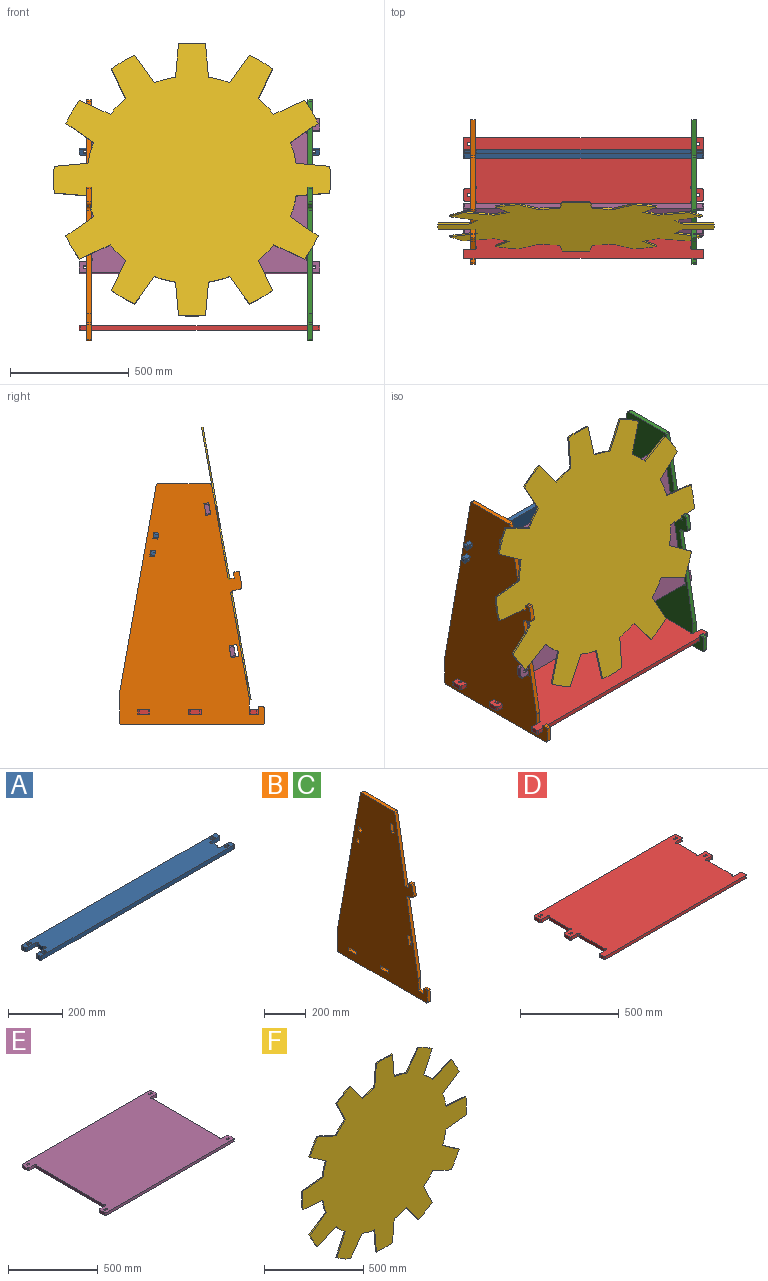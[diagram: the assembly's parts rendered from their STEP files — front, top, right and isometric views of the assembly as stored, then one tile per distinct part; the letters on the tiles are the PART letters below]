
ASSEMBLY  parts=6 mates=11
PART A: 50 faces, bbox 1016x101.6x19.1 mm
  f0: plane 1016x101.6mm, normal (0,0,-1), area 96811.6mm2, adj f2,f3,f4,f5,f6,f7,f8,f9
  f1: plane 1016x101.6mm, normal (0,0,1), area 96811.6mm2, adj f2,f3,f4,f5,f6,f7,f8,f9
  f2: plane 25.4x19.05mm, normal (1,0,0), area 483.9mm2, adj f0,f1,f3,f25
  f3: cylinder r=6.35mm len=19.05mm, axis (0,0,-1), area 380mm2, adj f0,f1,f2,f4
  f4: plane 44.45x19.05mm, normal (0,-1,0), area 846.8mm2, adj f0,f1,f3,f5
  f5: cylinder r=6.35mm len=19.05mm, axis (0,0,-1), area 190mm2, adj f0,f1,f4,f6
  f6: plane 19.05x12.7mm, normal (1,0,0), area 241.9mm2, adj f0,f1,f5,f7
  f7: cylinder r=6.35mm len=19.05mm, axis (0,0,-1), area 190mm2, adj f0,f1,f6,f8
  f8: plane 1003.3x19.05mm, normal (0,1,0), area 19112.9mm2, adj f0,f1,f7,f9
  f9: cylinder r=6.35mm len=19.05mm, axis (0,0,-1), area 190mm2, adj f0,f1,f8,f10
  f10: plane 19.05x12.7mm, normal (-1,0,0), area 241.9mm2, adj f0,f1,f9,f11
  f11: cylinder r=6.35mm len=19.05mm, axis (0,0,-1), area 190mm2, adj f0,f1,f10,f12
  f12: plane 44.45x19.05mm, normal (0,-1,0), area 846.8mm2, adj f0,f1,f11,f13
  f13: cylinder r=6.35mm len=19.05mm, axis (0,0,-1), area 380mm2, adj f0,f1,f12,f14
  f14: plane 25.4x19.05mm, normal (-1,0,0), area 483.9mm2, adj f0,f1,f13,f15
  f15: cylinder r=6.35mm len=19.05mm, axis (0,0,-1), area 380mm2, adj f0,f1,f14,f16
  f16: plane 44.45x19.05mm, normal (0,1,0), area 846.8mm2, adj f0,f1,f15,f17
  f17: cylinder r=6.35mm len=19.05mm, axis (0,0,-1), area 190mm2, adj f0,f1,f16,f18
  f18: plane 19.05x12.7mm, normal (-1,0,0), area 241.9mm2, adj f0,f1,f17,f19
  f19: cylinder r=6.35mm len=19.05mm, axis (0,0,-1), area 190mm2, adj f0,f1,f18,f20
  f20: plane 1003.3x19.05mm, normal (0,-1,0), area 19112.9mm2, adj f0,f1,f19,f21
  f21: cylinder r=6.35mm len=19.05mm, axis (0,0,-1), area 190mm2, adj f0,f1,f20,f22
  f22: plane 19.05x12.7mm, normal (1,0,0), area 241.9mm2, adj f0,f1,f21,f23
  f23: cylinder r=6.35mm len=19.05mm, axis (0,0,-1), area 190mm2, adj f0,f1,f22,f24
  f24: plane 44.45x19.05mm, normal (0,1,0), area 846.8mm2, adj f0,f1,f23,f25
  f25: cylinder r=6.35mm len=19.05mm, axis (0,0,-1), area 380mm2, adj f0,f1,f2,f24
  f26: plane 19.05x12.7mm, normal (0,-1,0), area 241.9mm2, adj f0,f1,f29,f49
  f27: plane 19.05x6.35mm, normal (1,0,0), area 121mm2, adj f0,f1,f48,f49
  f28: plane 19.05x12.7mm, normal (0,1,0), area 241.9mm2, adj f0,f1,f29,f48
  f29: cylinder r=6.35mm len=19.05mm, axis (0,0,1), area 380mm2, adj f0,f1,f26,f28
  f30: plane 19.05x6.35mm, normal (-1,0,0), area 121mm2, adj f0,f1,f46,f47
  f31: plane 19.05x12.7mm, normal (0,-1,0), area 241.9mm2, adj f0,f1,f32,f47
  f32: cylinder r=6.35mm len=19.05mm, axis (0,0,1), area 380mm2, adj f0,f1,f31,f33
  f33: plane 19.05x12.7mm, normal (0,1,0), area 241.9mm2, adj f0,f1,f32,f46
  f34: plane 19.05x6.35mm, normal (-1,0,0), area 121mm2, adj f0,f1,f44,f45
  f35: plane 19.05x12.7mm, normal (0,-1,0), area 241.9mm2, adj f0,f1,f36,f45
  f36: cylinder r=6.35mm len=19.05mm, axis (0,0,1), area 380mm2, adj f0,f1,f35,f37
  f37: plane 19.05x12.7mm, normal (0,1,0), area 241.9mm2, adj f0,f1,f36,f44
  f38: plane 19.05x12.7mm, normal (0,-1,0), area 241.9mm2, adj f0,f1,f41,f43
  f39: plane 19.05x6.35mm, normal (1,0,0), area 121mm2, adj f0,f1,f42,f43
  f40: plane 19.05x12.7mm, normal (0,1,0), area 241.9mm2, adj f0,f1,f41,f42
  f41: cylinder r=6.35mm len=19.05mm, axis (0,0,1), area 380mm2, adj f0,f1,f38,f40
  f42: cylinder r=1.59mm len=19.05mm, axis (0,0,1), area 95mm2, adj f0,f1,f39,f40
  f43: cylinder r=1.59mm len=19.05mm, axis (0,0,1), area 95mm2, adj f0,f1,f38,f39
  f44: cylinder r=1.59mm len=19.05mm, axis (0,0,1), area 95mm2, adj f0,f1,f34,f37
  f45: cylinder r=1.59mm len=19.05mm, axis (0,0,1), area 95mm2, adj f0,f1,f34,f35
  f46: cylinder r=1.59mm len=19.05mm, axis (0,0,1), area 95mm2, adj f0,f1,f30,f33
  f47: cylinder r=1.59mm len=19.05mm, axis (0,0,1), area 95mm2, adj f0,f1,f30,f31
  f48: cylinder r=1.59mm len=19.05mm, axis (0,0,1), area 95mm2, adj f0,f1,f27,f28
  f49: cylinder r=1.59mm len=19.05mm, axis (0,0,1), area 95mm2, adj f0,f1,f26,f27
PART B: 54 faces, bbox 19.1x609.6x1016 mm
  f0: plane 1016x609.6mm, normal (1,0,0), area 417121.7mm2, adj f2,f3,f4,f5,f6,f7,f8,f9
  f1: plane 1016x609.6mm, normal (-1,0,0), area 417121.7mm2, adj f2,f3,f4,f5,f6,f7,f8,f9
  f2: plane 50.8x19.05mm, normal (0,0,1), area 967.7mm2, adj f0,f1,f3,f28
  f3: plane 20.32x19.05mm, normal (0,1,0), area 387.1mm2, adj f0,f1,f2,f4
  f4: plane 50.8x19.05mm, normal (0,0,-1), area 967.7mm2, adj f0,f1,f3,f28
  f5: plane 19.05x19.05mm, normal (0,1,0), area 362.9mm2, adj f0,f1,f6,f26
  f6: plane 50.8x19.05mm, normal (0,0,-1), area 967.7mm2, adj f0,f1,f5,f7
  f7: plane 19.05x19.05mm, normal (0,-1,0), area 362.9mm2, adj f0,f1,f6,f26
  f8: plane 221.9x19.05mm, normal (0,0,1), area 4227.3mm2, adj f0,f1,f45,f53
  f9: plane 396.94x69.99mm, normal (0,-0.98,0.17), area 7678.4mm2, adj f0,f1,f10,f45
  f10: plane 25.01x19.05mm, normal (0,0.17,0.98), area 483.9mm2, adj f0,f1,f9,f11
  f11: plane 19.05x18.76mm, normal (0,0.98,-0.17), area 362.9mm2, adj f0,f1,f10,f46
  f12: plane 19.05x12.51mm, normal (0,0.17,0.98), area 241.9mm2, adj f0,f1,f46,f47
  f13: plane 56.28x19.05mm, normal (0,-0.98,0.17), area 1088.7mm2, adj f0,f1,f14,f47
  f14: cylinder r=12.7mm len=19.05mm, axis (-1,0,0), area 380mm2, adj f0,f1,f13,f15
  f15: plane 25.01x19.05mm, normal (0,-0.17,-0.98), area 483.9mm2, adj f0,f1,f14,f16
  f16: cylinder r=12.7mm len=19.05mm, axis (-1,0,0), area 380mm2, adj f0,f1,f15,f17
  f17: plane 435.93x76.87mm, normal (0,-0.98,0.17), area 8432.5mm2, adj f0,f1,f16,f18
  f18: cylinder r=12.7mm len=19.05mm, axis (-1,0,0), area 42.2mm2, adj f0,f1,f17,f19
  f19: plane 68.69x19.05mm, normal (0,-1,0), area 1308.6mm2, adj f0,f1,f18,f20
  f20: plane 38.1x19.05mm, normal (0,0,1), area 725.8mm2, adj f0,f1,f19,f21
  f21: plane 25.4x19.05mm, normal (0,1,0), area 483.9mm2, adj f0,f1,f20,f48
  f22: plane 19.05x12.7mm, normal (0,0,1), area 241.9mm2, adj f0,f1,f48,f49
  f23: plane 63.5x19.05mm, normal (0,-1,0), area 1209.7mm2, adj f0,f1,f49,f50
  f24: plane 596.9x19.05mm, normal (0,0,-1), area 11370.9mm2, adj f0,f1,f50,f51
  f25: plane 132.67x19.05mm, normal (0,1,0), area 2527.3mm2, adj f0,f1,f51,f52
  f26: plane 50.8x19.05mm, normal (0,0,1), area 967.7mm2, adj f0,f1,f5,f7
  f27: plane 870.63x153.52mm, normal (0,0.98,0.17), area 16841.4mm2, adj f0,f1,f52,f53
  f28: plane 20.32x19.05mm, normal (0,-1,0), area 387.1mm2, adj f0,f1,f2,f4
  f29: plane 20.01x19.05mm, normal (0,-0.17,-0.98), area 387.1mm2, adj f0,f1,f30,f32
  f30: plane 50.03x19.05mm, normal (0,0.98,-0.17), area 967.7mm2, adj f0,f1,f29,f31
  f31: plane 20.01x19.05mm, normal (0,0.17,0.98), area 387.1mm2, adj f0,f1,f30,f32
  f32: plane 50.03x19.05mm, normal (0,-0.98,0.17), area 967.7mm2, adj f0,f1,f29,f31
  f33: plane 20.01x19.05mm, normal (0,0.17,-0.98), area 387.1mm2, adj f0,f1,f34,f36
  f34: plane 25.01x19.05mm, normal (0,0.98,0.17), area 483.9mm2, adj f0,f1,f33,f35
  f35: plane 20.01x19.05mm, normal (0,-0.17,0.98), area 387.1mm2, adj f0,f1,f34,f36
  f36: plane 25.01x19.05mm, normal (0,-0.98,-0.17), area 483.9mm2, adj f0,f1,f33,f35
  f37: plane 20.01x19.05mm, normal (0,0.17,-0.98), area 387.1mm2, adj f0,f1,f38,f40
  f38: plane 25.01x19.05mm, normal (0,0.98,0.17), area 483.9mm2, adj f0,f1,f37,f39
  f39: plane 20.01x19.05mm, normal (0,-0.17,0.98), area 387.1mm2, adj f0,f1,f38,f40
  f40: plane 25.01x19.05mm, normal (0,-0.98,-0.17), area 483.9mm2, adj f0,f1,f37,f39
  f41: plane 20.01x19.05mm, normal (0,-0.17,-0.98), area 387.1mm2, adj f0,f1,f42,f44
  f42: plane 50.03x19.05mm, normal (0,0.98,-0.17), area 967.7mm2, adj f0,f1,f41,f43
  f43: plane 20.01x19.05mm, normal (0,0.17,0.98), area 387.1mm2, adj f0,f1,f42,f44
  f44: plane 50.03x19.05mm, normal (0,-0.98,0.17), area 967.7mm2, adj f0,f1,f41,f43
  f45: cylinder r=6.35mm len=19.05mm, axis (-1,0,0), area 168.9mm2, adj f0,f1,f8,f9
  f46: cylinder r=6.35mm len=19.05mm, axis (-1,0,0), area 190mm2, adj f0,f1,f11,f12
  f47: cylinder r=6.35mm len=19.05mm, axis (-1,0,0), area 190mm2, adj f0,f1,f12,f13
  f48: cylinder r=6.35mm len=19.05mm, axis (-1,0,0), area 190mm2, adj f0,f1,f21,f22
  f49: cylinder r=6.35mm len=19.05mm, axis (1,0,0), area 190mm2, adj f0,f1,f22,f23
  f50: cylinder r=6.35mm len=19.05mm, axis (1,0,0), area 190mm2, adj f0,f1,f23,f24
  f51: cylinder r=6.35mm len=19.05mm, axis (1,0,0), area 190mm2, adj f0,f1,f24,f25
  f52: cylinder r=6.35mm len=19.05mm, axis (1,0,0), area 21.1mm2, adj f0,f1,f25,f27
  f53: cylinder r=6.35mm len=19.05mm, axis (-1,0,0), area 168.9mm2, adj f0,f1,f8,f27
PART C: same geometry as B
PART D: 66 faces, bbox 1016x508x19.1 mm
  f0: plane 1016x508mm, normal (0,0,1), area 477168mm2, adj f2,f3,f4,f5,f6,f7,f8,f9
  f1: plane 1016x508mm, normal (0,0,-1), area 477168mm2, adj f2,f3,f4,f5,f6,f7,f8,f9
  f2: cylinder r=6.35mm len=19.05mm, axis (0,0,-1), area 380mm2, adj f0,f1,f3,f41
  f3: plane 139.7x19.05mm, normal (1,0,0), area 2661.3mm2, adj f0,f1,f2,f4
  f4: cylinder r=6.35mm len=19.05mm, axis (0,0,-1), area 380mm2, adj f0,f1,f3,f5
  f5: plane 44.45x19.05mm, normal (0,-1,0), area 846.8mm2, adj f0,f1,f4,f6
  f6: cylinder r=6.35mm len=19.05mm, axis (0,0,-1), area 190mm2, adj f0,f1,f5,f7
  f7: plane 38.1x19.05mm, normal (1,0,0), area 725.8mm2, adj f0,f1,f6,f8
  f8: cylinder r=6.35mm len=19.05mm, axis (0,0,-1), area 190mm2, adj f0,f1,f7,f9
  f9: plane 1003.3x19.05mm, normal (0,1,0), area 19112.9mm2, adj f0,f1,f8,f10
  f10: cylinder r=6.35mm len=19.05mm, axis (0,0,-1), area 190mm2, adj f0,f1,f9,f11
  f11: plane 38.1x19.05mm, normal (-1,0,0), area 725.8mm2, adj f0,f1,f10,f12
  f12: cylinder r=6.35mm len=19.05mm, axis (0,0,-1), area 190mm2, adj f0,f1,f11,f13
  f13: plane 44.45x19.05mm, normal (0,-1,0), area 846.8mm2, adj f0,f1,f12,f14
  f14: cylinder r=6.35mm len=19.05mm, axis (0,0,-1), area 380mm2, adj f0,f1,f13,f15
  f15: plane 139.7x19.05mm, normal (-1,0,0), area 2661.3mm2, adj f0,f1,f14,f16
  f16: cylinder r=6.35mm len=19.05mm, axis (0,0,-1), area 380mm2, adj f0,f1,f15,f17
  f17: plane 44.45x19.05mm, normal (0,1,0), area 846.8mm2, adj f0,f1,f16,f18
  f18: cylinder r=6.35mm len=19.05mm, axis (0,0,-1), area 190mm2, adj f0,f1,f17,f19
  f19: plane 38.1x19.05mm, normal (-1,0,0), area 725.8mm2, adj f0,f1,f18,f20
  f20: cylinder r=6.35mm len=19.05mm, axis (0,0,-1), area 190mm2, adj f0,f1,f19,f21
  f21: plane 44.45x19.05mm, normal (0,-1,0), area 846.8mm2, adj f0,f1,f20,f22
  f22: cylinder r=6.35mm len=19.05mm, axis (0,0,-1), area 380mm2, adj f0,f1,f21,f23
  f23: plane 177.8x19.05mm, normal (-1,0,0), area 3387.1mm2, adj f0,f1,f22,f24
  f24: cylinder r=6.35mm len=19.05mm, axis (0,0,-1), area 380mm2, adj f0,f1,f23,f25
  f25: plane 44.45x19.05mm, normal (0,1,0), area 846.8mm2, adj f0,f1,f24,f26
  f26: cylinder r=6.35mm len=19.05mm, axis (0,0,-1), area 190mm2, adj f0,f1,f25,f27
  f27: plane 25.4x19.05mm, normal (-1,0,0), area 483.9mm2, adj f0,f1,f26,f28
  f28: cylinder r=6.35mm len=19.05mm, axis (0,0,-1), area 190mm2, adj f0,f1,f27,f29
  f29: plane 1003.3x19.05mm, normal (0,-1,0), area 19112.9mm2, adj f0,f1,f28,f30
  f30: cylinder r=6.35mm len=19.05mm, axis (0,0,-1), area 190mm2, adj f0,f1,f29,f31
  f31: plane 25.4x19.05mm, normal (1,0,0), area 483.9mm2, adj f0,f1,f30,f32
  f32: cylinder r=6.35mm len=19.05mm, axis (0,0,-1), area 190mm2, adj f0,f1,f31,f33
  f33: plane 44.45x19.05mm, normal (0,1,0), area 846.8mm2, adj f0,f1,f32,f34
  f34: cylinder r=6.35mm len=19.05mm, axis (0,0,-1), area 380mm2, adj f0,f1,f33,f35
  f35: plane 177.8x19.05mm, normal (1,0,0), area 3387.1mm2, adj f0,f1,f34,f36
  f36: cylinder r=6.35mm len=19.05mm, axis (0,0,-1), area 380mm2, adj f0,f1,f35,f37
  f37: plane 44.45x19.05mm, normal (0,-1,0), area 846.8mm2, adj f0,f1,f36,f38
  f38: cylinder r=6.35mm len=19.05mm, axis (0,0,-1), area 190mm2, adj f0,f1,f37,f39
  f39: plane 38.1x19.05mm, normal (1,0,0), area 725.8mm2, adj f0,f1,f38,f40
  f40: cylinder r=6.35mm len=19.05mm, axis (0,0,-1), area 190mm2, adj f0,f1,f39,f41
  f41: plane 44.45x19.05mm, normal (0,1,0), area 846.8mm2, adj f0,f1,f2,f40
  f42: plane 19.05x12.7mm, normal (0,-1,0), area 241.9mm2, adj f0,f1,f43,f47
  f43: cylinder r=6.35mm len=19.05mm, axis (0,0,1), area 380mm2, adj f0,f1,f42,f44
  f44: plane 19.05x12.7mm, normal (0,1,0), area 241.9mm2, adj f0,f1,f43,f45
  f45: cylinder r=1.59mm len=19.05mm, axis (0,0,1), area 95mm2, adj f0,f1,f44,f46
  f46: plane 19.05x6.35mm, normal (-1,0,0), area 121mm2, adj f0,f1,f45,f47
  f47: cylinder r=1.59mm len=19.05mm, axis (0,0,1), area 95mm2, adj f0,f1,f42,f46
  f48: plane 19.05x12.7mm, normal (0,-1,0), area 241.9mm2, adj f0,f1,f49,f53
  f49: cylinder r=6.35mm len=19.05mm, axis (0,0,1), area 380mm2, adj f0,f1,f48,f50
  f50: plane 19.05x12.7mm, normal (0,1,0), area 241.9mm2, adj f0,f1,f49,f51
  f51: cylinder r=1.59mm len=19.05mm, axis (0,0,1), area 95mm2, adj f0,f1,f50,f52
  f52: plane 19.05x6.35mm, normal (-1,0,0), area 121mm2, adj f0,f1,f51,f53
  f53: cylinder r=1.59mm len=19.05mm, axis (0,0,1), area 95mm2, adj f0,f1,f48,f52
  f54: cylinder r=1.59mm len=19.05mm, axis (0,0,1), area 95mm2, adj f0,f1,f55,f59
  f55: plane 19.05x6.35mm, normal (1,0,0), area 121mm2, adj f0,f1,f54,f56
  f56: cylinder r=1.59mm len=19.05mm, axis (0,0,1), area 95mm2, adj f0,f1,f55,f57
  f57: plane 19.05x12.7mm, normal (0,1,0), area 241.9mm2, adj f0,f1,f56,f58
  f58: cylinder r=6.35mm len=19.05mm, axis (0,0,1), area 380mm2, adj f0,f1,f57,f59
  f59: plane 19.05x12.7mm, normal (0,-1,0), area 241.9mm2, adj f0,f1,f54,f58
  f60: cylinder r=1.59mm len=19.05mm, axis (0,0,1), area 95mm2, adj f0,f1,f61,f65
  f61: plane 19.05x12.7mm, normal (0,1,0), area 241.9mm2, adj f0,f1,f60,f62
  f62: cylinder r=6.35mm len=19.05mm, axis (0,0,1), area 380mm2, adj f0,f1,f61,f63
  f63: plane 19.05x12.7mm, normal (0,-1,0), area 241.9mm2, adj f0,f1,f62,f64
  f64: cylinder r=1.59mm len=19.05mm, axis (0,0,1), area 95mm2, adj f0,f1,f63,f65
  f65: plane 19.05x6.35mm, normal (1,0,0), area 121mm2, adj f0,f1,f60,f64
PART E: 50 faces, bbox 1016x660.4x19.1 mm
  f0: plane 1016x660.4mm, normal (0,0,1), area 612939.6mm2, adj f2,f3,f4,f5,f6,f7,f8,f9
  f1: plane 1016x660.4mm, normal (0,0,-1), area 612939.6mm2, adj f2,f3,f4,f5,f6,f7,f8,f9
  f2: plane 533.4x19.05mm, normal (1,0,0), area 10161.3mm2, adj f0,f1,f3,f25
  f3: cylinder r=6.35mm len=19.05mm, axis (0,0,-1), area 380mm2, adj f0,f1,f2,f4
  f4: plane 44.45x19.05mm, normal (0,-1,0), area 846.8mm2, adj f0,f1,f3,f5
  f5: cylinder r=6.35mm len=19.05mm, axis (0,0,-1), area 190mm2, adj f0,f1,f4,f6
  f6: plane 38.1x19.05mm, normal (1,0,0), area 725.8mm2, adj f0,f1,f5,f7
  f7: cylinder r=6.35mm len=19.05mm, axis (0,0,-1), area 190mm2, adj f0,f1,f6,f8
  f8: plane 1003.3x19.05mm, normal (0,1,0), area 19112.9mm2, adj f0,f1,f7,f9
  f9: cylinder r=6.35mm len=19.05mm, axis (0,0,-1), area 190mm2, adj f0,f1,f8,f10
  f10: plane 38.1x19.05mm, normal (-1,0,0), area 725.8mm2, adj f0,f1,f9,f11
  f11: cylinder r=6.35mm len=19.05mm, axis (0,0,-1), area 190mm2, adj f0,f1,f10,f12
  f12: plane 44.45x19.05mm, normal (0,-1,0), area 846.8mm2, adj f0,f1,f11,f13
  f13: cylinder r=6.35mm len=19.05mm, axis (0,0,-1), area 380mm2, adj f0,f1,f12,f14
  f14: plane 533.4x19.05mm, normal (-1,0,0), area 10161.3mm2, adj f0,f1,f13,f15
  f15: cylinder r=6.35mm len=19.05mm, axis (0,0,-1), area 380mm2, adj f0,f1,f14,f16
  f16: plane 44.45x19.05mm, normal (0,1,0), area 846.8mm2, adj f0,f1,f15,f17
  f17: cylinder r=6.35mm len=19.05mm, axis (0,0,-1), area 190mm2, adj f0,f1,f16,f18
  f18: plane 38.1x19.05mm, normal (-1,0,0), area 725.8mm2, adj f0,f1,f17,f19
  f19: cylinder r=6.35mm len=19.05mm, axis (0,0,-1), area 190mm2, adj f0,f1,f18,f20
  f20: plane 1003.3x19.05mm, normal (0,-1,0), area 19112.9mm2, adj f0,f1,f19,f21
  f21: cylinder r=6.35mm len=19.05mm, axis (0,0,-1), area 190mm2, adj f0,f1,f20,f22
  f22: plane 38.1x19.05mm, normal (1,0,0), area 725.8mm2, adj f0,f1,f21,f23
  f23: cylinder r=6.35mm len=19.05mm, axis (0,0,-1), area 190mm2, adj f0,f1,f22,f24
  f24: plane 44.45x19.05mm, normal (0,1,0), area 846.8mm2, adj f0,f1,f23,f25
  f25: cylinder r=6.35mm len=19.05mm, axis (0,0,-1), area 380mm2, adj f0,f1,f2,f24
  f26: cylinder r=6.35mm len=19.05mm, axis (0,0,-1), area 380mm2, adj f0,f1,f27,f29
  f27: plane 19.05x12.7mm, normal (0,-1,0), area 241.9mm2, adj f0,f1,f26,f28
  f28: cylinder r=1.59mm len=19.05mm, axis (0,0,-1), area 95mm2, adj f0,f1,f27,f30
  f29: plane 19.05x12.7mm, normal (0,1,0), area 241.9mm2, adj f0,f1,f26,f31
  f30: plane 19.05x6.35mm, normal (-1,0,0), area 121mm2, adj f0,f1,f28,f31
  f31: cylinder r=1.59mm len=19.05mm, axis (0,0,-1), area 95mm2, adj f0,f1,f29,f30
  f32: cylinder r=6.35mm len=19.05mm, axis (0,0,-1), area 380mm2, adj f0,f1,f33,f35
  f33: plane 19.05x12.7mm, normal (0,-1,0), area 241.9mm2, adj f0,f1,f32,f34
  f34: cylinder r=1.59mm len=19.05mm, axis (0,0,-1), area 95mm2, adj f0,f1,f33,f36
  f35: plane 19.05x12.7mm, normal (0,1,0), area 241.9mm2, adj f0,f1,f32,f37
  f36: plane 19.05x6.35mm, normal (-1,0,0), area 121mm2, adj f0,f1,f34,f37
  f37: cylinder r=1.59mm len=19.05mm, axis (0,0,-1), area 95mm2, adj f0,f1,f35,f36
  f38: cylinder r=6.35mm len=19.05mm, axis (0,0,-1), area 380mm2, adj f0,f1,f39,f43
  f39: plane 19.05x12.7mm, normal (0,1,0), area 241.9mm2, adj f0,f1,f38,f40
  f40: cylinder r=1.59mm len=19.05mm, axis (0,0,-1), area 95mm2, adj f0,f1,f39,f41
  f41: plane 19.05x6.35mm, normal (1,0,0), area 121mm2, adj f0,f1,f40,f42
  f42: cylinder r=1.59mm len=19.05mm, axis (0,0,-1), area 95mm2, adj f0,f1,f41,f43
  f43: plane 19.05x12.7mm, normal (0,-1,0), area 241.9mm2, adj f0,f1,f38,f42
  f44: cylinder r=6.35mm len=19.05mm, axis (0,0,-1), area 380mm2, adj f0,f1,f45,f49
  f45: plane 19.05x12.7mm, normal (0,1,0), area 241.9mm2, adj f0,f1,f44,f46
  f46: cylinder r=1.59mm len=19.05mm, axis (0,0,-1), area 95mm2, adj f0,f1,f45,f47
  f47: plane 19.05x6.35mm, normal (1,0,0), area 121mm2, adj f0,f1,f46,f48
  f48: cylinder r=1.59mm len=19.05mm, axis (0,0,-1), area 95mm2, adj f0,f1,f47,f49
  f49: plane 19.05x12.7mm, normal (0,-1,0), area 241.9mm2, adj f0,f1,f44,f48
PART F: 50 faces, bbox 1168.4x6.4x1168.4 mm
  f0: plane 117.08x81.98mm, normal (0.82,0,-0.57), area 907.6mm2, adj f1,f47,f48,f49
  f1: cylinder r=444.5mm len=89.62mm, axis (0,1,0), area 590.2mm2, adj f0,f2,f48,f49
  f2: plane 142.38x12.46mm, normal (-1,0,-0.09), area 907.6mm2, adj f1,f3,f48,f49
  f3: cylinder r=584.2mm len=114.3mm, axis (0,1,0), area 727mm2, adj f2,f4,f48,f49
  f4: plane 142.38x12.46mm, normal (1,0,-0.09), area 907.6mm2, adj f3,f5,f48,f49
  f5: cylinder r=444.5mm len=89.62mm, axis (0,1,0), area 590.2mm2, adj f4,f6,f48,f49
  f6: plane 117.08x81.98mm, normal (-0.82,0,-0.57), area 907.6mm2, adj f5,f7,f48,f49
  f7: cylinder r=584.2mm len=98.99mm, axis (0,1,0), area 727mm2, adj f6,f8,f48,f49
  f8: plane 129.53x60.4mm, normal (0.91,0,0.42), area 907.6mm2, adj f7,f9,f48,f49
  f9: cylinder r=444.5mm len=65.61mm, axis (0,1,0), area 590.2mm2, adj f8,f10,f48,f49
  f10: plane 129.53x60.4mm, normal (-0.42,0,-0.91), area 907.6mm2, adj f9,f11,f48,f49
  f11: cylinder r=584.2mm len=98.99mm, axis (0,1,0), area 727mm2, adj f10,f12,f48,f49
  f12: plane 117.08x81.98mm, normal (0.57,0,0.82), area 907.6mm2, adj f11,f13,f48,f49
  f13: cylinder r=444.5mm len=89.62mm, axis (0,1,0), area 590.2mm2, adj f12,f14,f48,f49
  f14: plane 142.38x12.46mm, normal (0.09,0,-1), area 907.6mm2, adj f13,f15,f48,f49
  f15: cylinder r=584.2mm len=114.3mm, axis (0,1,0), area 727mm2, adj f14,f16,f48,f49
  f16: plane 142.38x12.46mm, normal (0.09,0,1), area 907.6mm2, adj f15,f17,f48,f49
  f17: cylinder r=444.5mm len=89.62mm, axis (0,1,0), area 590.2mm2, adj f16,f18,f48,f49
  f18: plane 117.08x81.98mm, normal (0.57,0,-0.82), area 907.6mm2, adj f17,f19,f48,f49
  f19: cylinder r=584.2mm len=98.99mm, axis (0,1,0), area 727mm2, adj f18,f20,f48,f49
  f20: plane 129.53x60.4mm, normal (-0.42,0,0.91), area 907.6mm2, adj f19,f21,f48,f49
  f21: cylinder r=444.5mm len=65.61mm, axis (0,1,0), area 590.2mm2, adj f20,f22,f48,f49
  f22: plane 129.53x60.4mm, normal (0.91,0,-0.42), area 907.6mm2, adj f21,f23,f48,f49
  f23: cylinder r=584.2mm len=98.99mm, axis (0,1,0), area 727mm2, adj f22,f24,f48,f49
  f24: plane 117.08x81.98mm, normal (-0.82,0,0.57), area 907.6mm2, adj f23,f25,f48,f49
  f25: cylinder r=444.5mm len=89.62mm, axis (0,1,0), area 590.2mm2, adj f24,f26,f48,f49
  f26: plane 142.38x12.46mm, normal (1,0,0.09), area 907.6mm2, adj f25,f27,f48,f49
  f27: cylinder r=584.2mm len=114.3mm, axis (0,1,0), area 727mm2, adj f26,f28,f48,f49
  f28: plane 142.38x12.46mm, normal (-1,0,0.09), area 907.6mm2, adj f27,f29,f48,f49
  f29: cylinder r=444.5mm len=89.62mm, axis (0,1,0), area 590.2mm2, adj f28,f30,f48,f49
  f30: plane 117.08x81.98mm, normal (0.82,0,0.57), area 907.6mm2, adj f29,f31,f48,f49
  f31: cylinder r=584.2mm len=98.99mm, axis (0,1,0), area 727mm2, adj f30,f32,f48,f49
  f32: plane 129.53x60.4mm, normal (-0.91,0,-0.42), area 907.6mm2, adj f31,f33,f48,f49
  f33: cylinder r=444.5mm len=65.61mm, axis (0,1,0), area 590.2mm2, adj f32,f34,f48,f49
  f34: plane 129.53x60.4mm, normal (0.42,0,0.91), area 907.6mm2, adj f33,f35,f48,f49
  f35: cylinder r=584.2mm len=98.99mm, axis (0,1,0), area 727mm2, adj f34,f36,f48,f49
  f36: plane 117.08x81.98mm, normal (-0.57,0,-0.82), area 907.6mm2, adj f35,f37,f48,f49
  f37: cylinder r=444.5mm len=89.62mm, axis (0,1,0), area 590.2mm2, adj f36,f38,f48,f49
  f38: plane 142.38x12.46mm, normal (-0.09,0,1), area 907.6mm2, adj f37,f39,f48,f49
  f39: cylinder r=584.2mm len=114.3mm, axis (0,1,0), area 727mm2, adj f38,f40,f48,f49
  f40: plane 142.38x12.46mm, normal (-0.09,0,-1), area 907.6mm2, adj f39,f41,f48,f49
  f41: cylinder r=444.5mm len=89.62mm, axis (0,1,0), area 590.2mm2, adj f40,f42,f48,f49
  f42: plane 117.08x81.98mm, normal (-0.57,0,0.82), area 907.6mm2, adj f41,f43,f48,f49
  f43: cylinder r=584.2mm len=98.99mm, axis (0,1,0), area 727mm2, adj f42,f44,f48,f49
  f44: plane 129.53x60.4mm, normal (0.42,0,-0.91), area 907.6mm2, adj f43,f45,f48,f49
  f45: cylinder r=444.5mm len=65.61mm, axis (0,1,0), area 590.2mm2, adj f44,f46,f48,f49
  f46: plane 129.53x60.4mm, normal (-0.91,0,0.42), area 907.6mm2, adj f45,f47,f48,f49
  f47: cylinder r=584.2mm len=98.99mm, axis (0,1,0), area 727mm2, adj f0,f46,f48,f49
  f48: plane 1168.4x1168.4mm, normal (0,-1,0), area 833739.4mm2, adj f0,f1,f2,f3,f4,f5,f6,f7
  f49: plane 1168.4x1168.4mm, normal (0,1,0), area 833739.4mm2, adj f0,f1,f2,f3,f4,f5,f6,f7
PLACE A rot(axis=(1,0,0),100deg) t=(27.6,255.94,762.67)mm
PLACE B t=(-448.65,443.44,1.44)mm
PLACE C t=(484.8,443.44,1.44)mm
PLACE D t=(27.6,-45.51,45.89)mm
PLACE E rot(axis=(-1,0,0),100deg) t=(27.6,-38.76,612.58)mm
PLACE F rot(axis=(-1,0,0),10deg) t=(-4.09,-53.99,679.83)mm
MATE planar E.f16 <-> B.f43  axis (0,-0.17,-0.98) through (-451.83,19.13,886.08)mm
MATE planar B.f17 <-> C.f17  axis (0,-0.98,0.17) through (-439.13,-114.83,334.75)mm
MATE planar A.f2 <-> C.f1  axis (1,0,0) through (484.8,246.56,761.01)mm
MATE planar D.f35 <-> C.f1  axis (1,0,0) through (484.8,-51.86,55.41)mm
MATE planar E.f0 <-> B.f44  axis (0,0.98,-0.17) through (27.6,-20,609.27)mm
MATE planar D.f17 <-> B.f28  axis (0,1,0) through (-451.83,100.54,55.41)mm
MATE planar D.f1 <-> B.f2  axis (0,0,-1) through (27.6,62.9,45.89)mm
MATE planar A.f1 <-> C.f38  axis (0,-0.98,-0.17) through (27.6,237.18,759.36)mm
MATE planar A.f8 <-> C.f33  axis (0,-0.17,0.98) through (27.6,237.74,811.04)mm
MATE planar F.f1 <-> C.f9  axis (0,0.98,-0.17) through (-4.09,-53.99,679.83)mm
MATE planar B.f24 <-> C.f24  axis (0,0,-1) through (-439.13,87.84,1.44)mm
